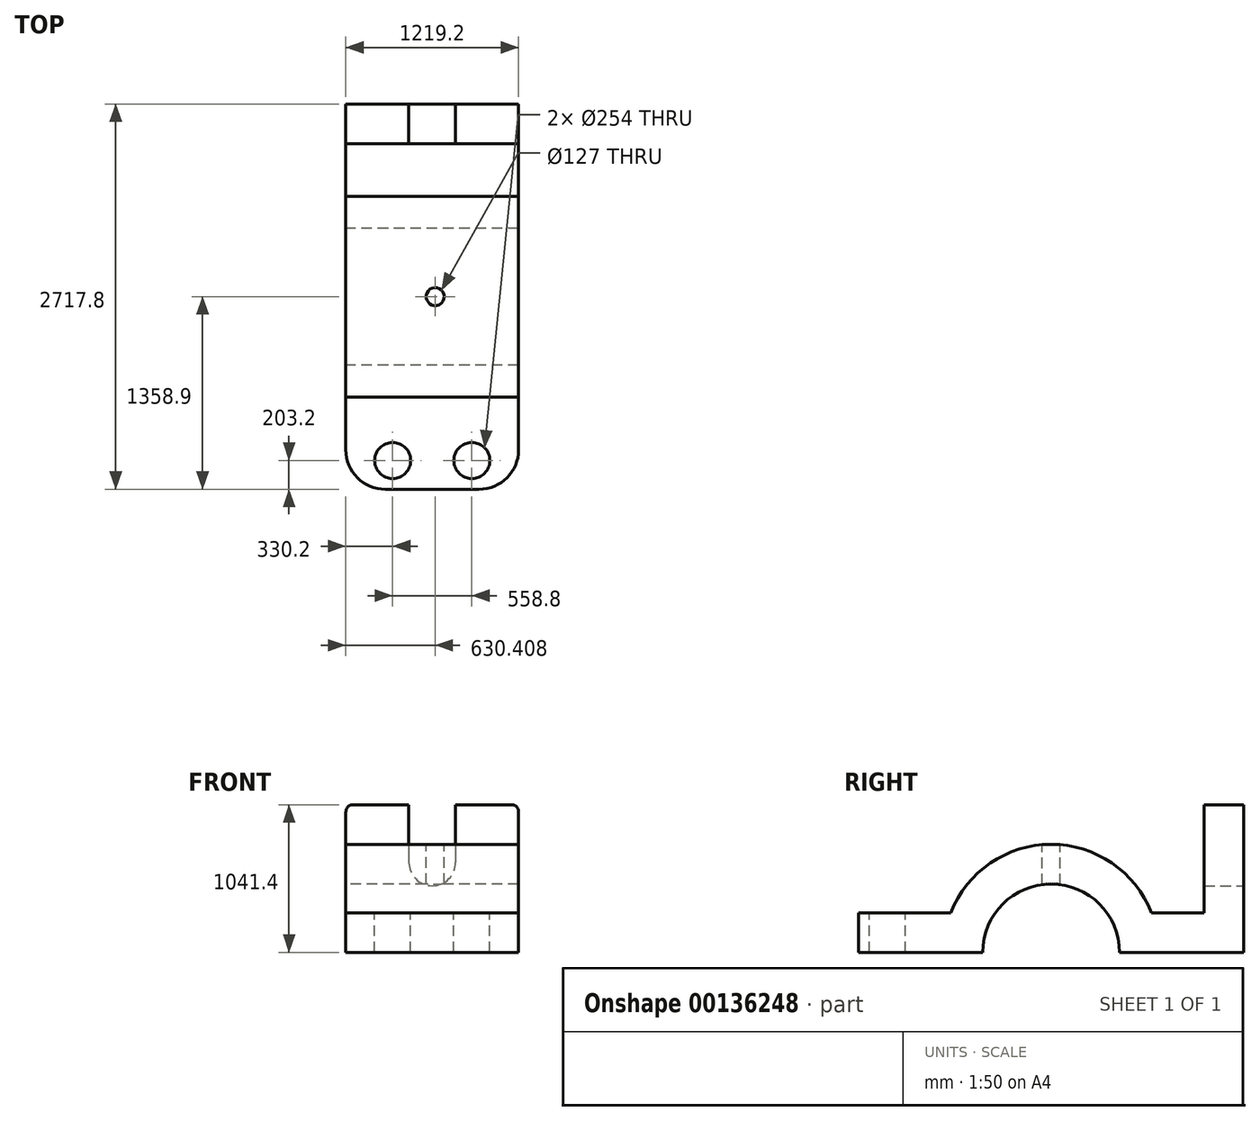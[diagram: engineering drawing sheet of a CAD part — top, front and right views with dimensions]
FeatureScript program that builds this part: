
annotation { "Feature Type Name" : "Feature", "Feature Type Description" : "" }
export const myFeature = defineFeature(function(context is Context, id is Id, definition is map)
    precondition{}
    {
        {
            var Q0;
            Q0=qCreatedBy(makeId("Right.planeOp"),FACE);
            var sketch = newSketch(context, id + "F0", { "sketchPlane" : qUnion([Q0])});
            skLineSegment(sketch, "E0", {"start": v(0, 0) * mm, "end": v(596.9, 0) * mm});
            skLineSegment(sketch, "E1", {"start": v(2120.9, 0) * mm, "end": v(2717.8, 0) * mm});
            skArc(sketch, "E2", {"start": v(2067.83, 279.4) * mm, "mid": v(1358.9, 762) * mm, "end": v(649.97, 279.4) * mm});
            skLineSegment(sketch, "E3.0", {"start": v(0, 279.4) * mm, "end": v(649.97, 279.4) * mm});
            skLineSegment(sketch, "E4.0", {"start": v(2067.83, 279.4) * mm, "end": v(2438.4, 279.4) * mm});
            skLineSegment(sketch, "E5", {"start": v(0, 279.4) * mm, "end": v(0, 0) * mm});
            skLineSegment(sketch, "E6", {"start": v(2717.8, 279.4) * mm, "end": v(2717.8, 0) * mm});
            skArc(sketch, "E7", {"start": v(1841.12, 0) * mm, "mid": v(1358.9, 482.22) * mm, "end": v(876.68, 0) * mm});
            skLineSegment(sketch, "E8", {"start": v(2717.8, 0) * mm, "end": v(2438.4, 0) * mm});
            skLineSegment(sketch, "E9", {"start": v(2438.4, 279.4) * mm, "end": v(2438.4, 1041.4) * mm});
            skLineSegment(sketch, "E10.0", {"start": v(2717.8, 0) * mm, "end": v(2717.8, 1041.4) * mm});
            skPoint(sketch, "E11.end.orphan", {"position": v(1841.12, 0) * mm});
            skPoint(sketch, "E12.orphan", {"position": v(876.68, 0) * mm});
            skLineSegment(sketch, "E13", {"start": v(596.9, 0) * mm, "end": v(876.68, 0) * mm});
            skLineSegment(sketch, "E14", {"start": v(1841.12, 0) * mm, "end": v(2120.9, 0) * mm});
            skLineSegment(sketch, "E15", {"start": v(2438.4, 1041.4) * mm, "end": v(2717.8, 1041.4) * mm});
            skSolve(sketch);
        }
        {
            var Q0;
            Q0 = qSketchRegion(id + "F0", true);
            extrude(context, id + "F1", {"entities" : qUnion([Q0]), "endBound" : BoundingType.SYMMETRIC, "depth" : 1219.2 * mm});
        }
        {
            var Q0;
            Q0=makeQuery(id+"F1.opExtrude","CAP_EDGE",EDGE,{"disambiguationData":[OSD([sQuery(id+"F0.wireOp",EDGE,"E15")])],"isStart":false});
            var Q1;
            Q1=makeQuery(id+"F1.opExtrude","CAP_EDGE",EDGE,{"disambiguationData":[OSD([sQuery(id+"F0.wireOp",EDGE,"E15")])],"isStart":true});
            fillet(context, id + "F2", {"entities" : qUnion([Q0, Q1]), "radius" : 50.8 * mm, "tangentPropagation" : true, "allowEdgeOverflow" : false});
        }
        {
            var Q0;
            Q0=makeQuery(id+"F1.opExtrude","SWEPT_FACE",FACE,{"disambiguationData":[OSD([sQuery(id+"F0.wireOp",EDGE,"E10.0")])]});
            var sketch = newSketch(context, id + "F3", { "sketchPlane" : qUnion([Q0])});
            skLineSegment(sketch, "E16", {"start": v(-165.1, 1041.4) * mm, "end": v(165.1, 1041.4) * mm});
            skLineSegment(sketch, "E17", {"start": v(-165.1, 1041.4) * mm, "end": v(-165.1, 635) * mm});
            skLineSegment(sketch, "E18", {"start": v(165.1, 1041.4) * mm, "end": v(165.1, 635) * mm});
            skArc(sketch, "E19", {"start": v(-165.1, 635) * mm, "mid": v(0, 469.9) * mm, "end": v(165.1, 635) * mm});
            skSolve(sketch);
        }
        {
            var Q0;
            Q0 = qSketchRegion(id + "F3", true);
            var Q1;
            Q1=makeQuery(id+"F1.opExtrude","SWEPT_FACE",FACE,{"disambiguationData":[OSD([sQuery(id+"F0.wireOp",EDGE,"E9")])]});
            extrude(context, id + "F4", {"entities" : qUnion([Q0]), "operationType" : NewBodyOperationType.REMOVE, "endBound" : BoundingType.UP_TO_SURFACE, "oppositeDirection" : true, "endBoundEntityFace" : qUnion([Q1]), "depth" : 25.4 * mm});
        }
        {
            var Q0;
            Q0=makeQuery(id+"F1.opExtrude","SWEPT_FACE",FACE,{"disambiguationData":[OSD([sQuery(id+"F0.wireOp",EDGE,"E3.0")])]});
            var sketch = newSketch(context, id + "F5", { "sketchPlane" : qUnion([Q0])});
            skCircle(sketch, "E20", {"center": v(-279.4, 203.2) * mm, "radius": 127 * mm});
            skCircle(sketch, "E21", {"center": v(279.4, 203.2) * mm, "radius": 127 * mm});
            skSolve(sketch);
        }
        {
            var Q0;
            Q0 = qSketchRegion(id + "F5", true);
            extrude(context, id + "F6", {"entities" : qUnion([Q0]), "operationType" : NewBodyOperationType.REMOVE, "endBound" : BoundingType.THROUGH_ALL, "oppositeDirection" : true, "depth" : 25.4 * mm});
        }
        {
            var Q0;
            Q0 = qSketchRegion(id + "F5", true);
            extrude(context, id + "F7", {"entities" : qUnion([Q0]), "operationType" : NewBodyOperationType.REMOVE, "depth" : 25.4 * mm});
        }
        {
            var Q0;
            Q0=makeQuery(id+"F1.opExtrude","CAP_EDGE",EDGE,{"disambiguationData":[OSD([sQuery(id+"F0.wireOp",EDGE,"E5")])],"isStart":false});
            var Q1;
            Q1=makeQuery(id+"F1.opExtrude","CAP_EDGE",EDGE,{"disambiguationData":[OSD([sQuery(id+"F0.wireOp",EDGE,"E5")])],"isStart":true});
            fillet(context, id + "F8", {"entities" : qUnion([Q0, Q1]), "radius" : 279.4 * mm, "tangentPropagation" : true, "allowEdgeOverflow" : false});
        }
        {
            var Q0;
            Q0=makeQuery(id+"F1.opExtrude","SWEPT_FACE",FACE,{"disambiguationData":[OSD([sQuery(id+"F0.wireOp",EDGE,"E0"),sQuery(id+"F0.wireOp",EDGE,"E13")])]});
            cPlane(context, id + "F9", {"entities" : qUnion([Q0]), "cplaneType" : CPlaneType.OFFSET, "offset" : 762 * mm, "oppositeDirection" : true, "width" : 152.4 * mm, "height" : 152.4 * mm});
        }
        {
            var Q0;
            Q0=qCreatedBy(id+"F9.planeOp",FACE);
            var sketch = newSketch(context, id + "F10", { "sketchPlane" : qUnion([Q0])});
            skCircle(sketch, "E22", {"center": v(20.8, -1358.9) * mm, "radius": 63.5 * mm});
            skSolve(sketch);
        }
        {
            var Q0;
            Q0 = qSketchRegion(id + "F10", true);
            extrude(context, id + "F11", {"entities" : qUnion([Q0]), "operationType" : NewBodyOperationType.REMOVE, "endBound" : BoundingType.THROUGH_ALL, "depth" : 25.4 * mm});
        }
    });
